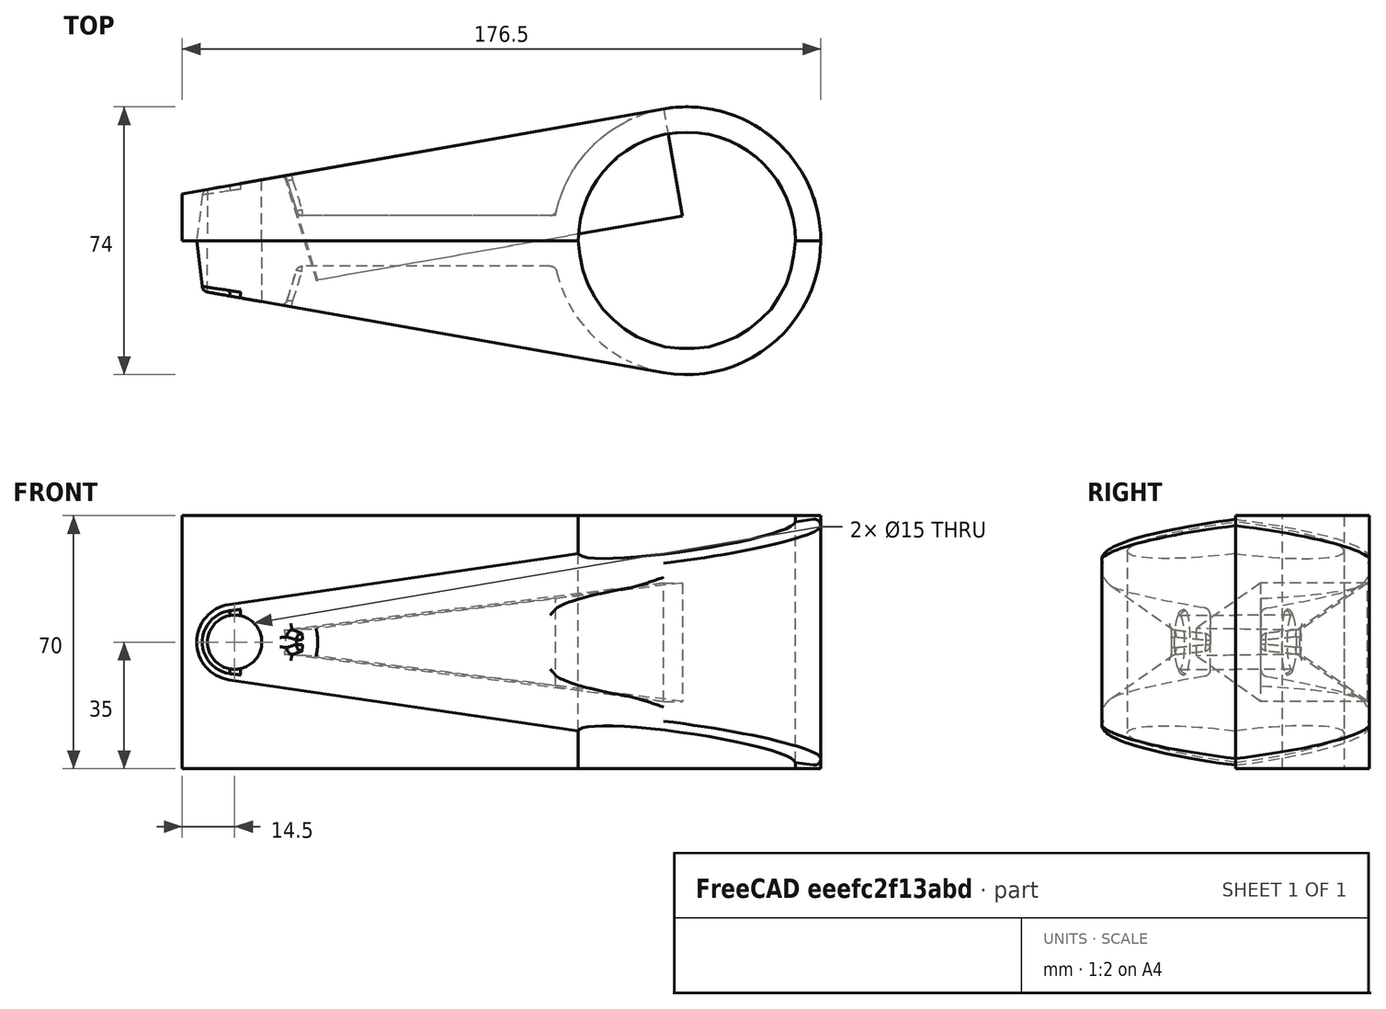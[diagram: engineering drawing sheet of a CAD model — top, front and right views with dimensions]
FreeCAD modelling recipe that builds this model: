
FCSTD DOCUMENT  (FreeCAD 1.0R39319 (Git))
Label: Mania2002-S2-1
License: All rights reserved
LicenseURL: https://en.wikipedia.org/wiki/All_rights_reserved
objects: Sketcher::SketchObject×6, PartDesign::Pad×4, PartDesign::Body×4, PartDesign::Boolean×3, PartDesign::Draft×3, PartDesign::SubShapeBinder×2, Spreadsheet::Sheet×1, PartDesign::Pocket×1, PartDesign::Fillet×1, PartDesign::Mirrored×1
note: 53 computed .brp shape members not serialized (recipe doc carries the construction recipe); baked Part::Feature solids carry a one-line shape summary decoded from their .brp

FEATURE [Spreadsheet::Sheet] Spreadsheet
  cells = A1='MainDiameter; B1(LargeDiameter)=60; A2='SubDiameter; B2(SmallDiameter)=15; A3='Length; B3(Distance)=125; A4='Thickness; B4(Thickness)=7; A5='Angle; B5=7; A6='Slope; B6(Slope)=10; A7='Fillet; B7(Fillet)=3
FEATURE [Sketcher::SketchObject] Sketch  label="Main outline"
  ArcFitTolerance = 1e-06
  AttachmentSupport = -> [XY_Plane]
  FullyConstrained = true
  MakeInternals = false
  MapMode = 5
  expr: Constraints[0] = Spreadsheet.B6
  expr: Constraints[11] = Spreadsheet.B3
  expr: Constraints[12] = Spreadsheet.B2 / 2 + Spreadsheet.B4
  expr: Constraints[14] = Spreadsheet.LargeDiameter / 2
  expr: Constraints[17] = Spreadsheet.Thickness
  sketch-geometry (7):
    g0: ArcOfCircle CenterX=0 CenterY=0 CenterZ=0 NormalX=0 NormalY=0 NormalZ=1 AngleXU=0 Radius=37 StartAngle=0 EndAngle=1.74533
    g1: LineSegment StartX=-6.42498 StartY=36.4379 StartZ=0 EndX=-139.5 EndY=12.9732 EndZ=0
    g2: LineSegment StartX=-139.5 StartY=12.9732 StartZ=0 EndX=-139.5 EndY=0 EndZ=0
    g3: LineSegment StartX=-139.5 StartY=0 StartZ=0 EndX=-125 EndY=0 EndZ=0
    g4: LineSegment StartX=-125 StartY=0 StartZ=0 EndX=-30 EndY=0 EndZ=0
    g5: LineSegment StartX=30 StartY=0 StartZ=0 EndX=37 EndY=0 EndZ=0
    g6: ArcOfCircle CenterX=0 CenterY=0 CenterZ=0 NormalX=0 NormalY=0 NormalZ=1 AngleXU=0 Radius=30 StartAngle=0 EndAngle=3.14159
  constraints (20):
    c: Angle(g-1,g1) = 0.174533
    c: Tangent(g0,g1) = -1.5708
    c: Coincident(g0,g-1)
    c: Coincident(g2,g1)
    c: Vertical(g2)
    c: PointOnObject(g2,g-1)
    c: PointOnObject(g0,g-1)
    c: Coincident(g2,g3)
    c: PointOnObject(g3,g-1)
    c: Coincident(g3,g4)
    c: Coincident(g5,g0)
    c: DistanceX(g3,g-1) = 125
    c: DistanceX(g3,g3) = 14.5
    c: Coincident(g6,g0)
    c: Radius(g6) = 30
    c: Coincident(g5,g6)
    c: PointOnObject(g5,g-1)
    c: Distance(g5,g5) = 7
    c: Coincident(g4,g6)
    c: PointOnObject(g4,g-1)
FEATURE [Sketcher::SketchObject] Sketch001  label="base"
  ArcFitTolerance = 1e-06
  AttachmentSupport = -> [XY_Plane]
  FullyConstrained = true
  MakeInternals = false
  MapMode = 5
  expr: Constraints[0] = Spreadsheet.Slope
  expr: Constraints[11] = Spreadsheet.B3
  expr: Constraints[12] = Spreadsheet.B2 / 2 + Spreadsheet.B4
  expr: Constraints[14] = Spreadsheet.LargeDiameter / 2
  expr: Constraints[17] = Spreadsheet.Thickness
  sketch-geometry (7):
    g0: ArcOfCircle CenterX=0 CenterY=0 CenterZ=0 NormalX=0 NormalY=0 NormalZ=1 AngleXU=0 Radius=37 StartAngle=0 EndAngle=1.74533
    g1: LineSegment StartX=-6.42498 StartY=36.4379 StartZ=0 EndX=-139.5 EndY=12.9732 EndZ=0
    g2: LineSegment StartX=-139.5 StartY=12.9732 StartZ=0 EndX=-139.5 EndY=0 EndZ=0
    g3: LineSegment StartX=-139.5 StartY=0 StartZ=0 EndX=-125 EndY=0 EndZ=0
    g4: LineSegment StartX=-125 StartY=0 StartZ=0 EndX=-30 EndY=3.7e-15 EndZ=0
    g5: LineSegment StartX=30 StartY=0 StartZ=0 EndX=37 EndY=0 EndZ=0
    g6: ArcOfCircle CenterX=0 CenterY=0 CenterZ=0 NormalX=0 NormalY=0 NormalZ=1 AngleXU=0 Radius=30 StartAngle=0 EndAngle=3.14159
  constraints (20):
    c: Angle(g-1,g1) = 0.174533
    c: Tangent(g0,g1) = -1.5708
    c: Coincident(g0,g-1)
    c: Coincident(g2,g1)
    c: Vertical(g2)
    c: PointOnObject(g2,g-1)
    c: PointOnObject(g0,g-1)
    c: Coincident(g2,g3)
    c: PointOnObject(g3,g-1)
    c: Coincident(g3,g4)
    c: Coincident(g5,g0)
    c: DistanceX(g3,g-1) = 125
    c: DistanceX(g3,g3) = 14.5
    c: Coincident(g6,g0)
    c: Radius(g6) = 30
    c: Coincident(g5,g6)
    c: PointOnObject(g5,g-1)
    c: Distance(g5,g5) = 7
    c: Coincident(g4,g6)
    c: PointOnObject(g4,g-1)
FEATURE [PartDesign::Pad] Pad
  Direction = (0,0,1)
  Length = 70
  Length2 = 10
  Midplane = true
  Profile = -> Sketch001
  ReferenceAxis = -> Sketch001 [N_Axis]
  Refine = true
  Suppressed = false
  Type = 0
FEATURE [PartDesign::Body] Body
  AllowCompound = false
  Group = -> [Sketch,Sketch001,Pad]
  Origin = -> Origin
  Tip = -> Pad
FEATURE [Sketcher::SketchObject] Sketch003
  ArcFitTolerance = 1e-06
  AttachmentSupport = -> [XZ_Plane001]
  FullyConstrained = true
  MakeInternals = false
  MapMode = 5
  Placement = pos=(0,0,0) rot=(1,0,0;1.5708rad)
  expr: Constraints[5] = Spreadsheet.Distance
  sketch-geometry (4):
    g0: LineSegment StartX=42 StartY=35 StartZ=0 EndX=42 EndY=-35 EndZ=0
    g1: LineSegment StartX=42 StartY=-35 StartZ=0 EndX=-126.517 EndY=-10.3898 EndZ=0
    g2: ArcOfCircle CenterX=-125 CenterY=0 CenterZ=0 NormalX=0 NormalY=0 NormalZ=1 AngleXU=0 Radius=10.5 StartAngle=1.71581 EndAngle=4.56737
    g3: LineSegment StartX=-126.517 StartY=10.3898 StartZ=0 EndX=42 EndY=35 EndZ=0
  constraints (9):
    c: Coincident(g-3,g0)
    c: Coincident(g0,g-3)
    c: Coincident(g0,g1)
    c: Coincident(g3,g0)
    c: Tangent(g2,g-4)
    c: DistanceX(g2,g-1) = 125
    c: Tangent(g2,g3) = 1.5708
    c: Tangent(g1,g2) = 1.5708
    c: PointOnObject(g2,g-1)
FEATURE [PartDesign::Pad] Pad002
  Direction = (0,-1,2e-16)
  Length = 50
  Length2 = 10
  Placement = pos=(0,0,0) rot=(1,0,0;1.5708rad)
  Profile = -> Sketch003
  ReferenceAxis = -> Sketch003 [N_Axis]
  Refine = true
  Reversed = true
  Suppressed = false
  Type = 0
FEATURE [PartDesign::Boolean] Boolean
  BaseFeature = -> Pad002
  Group = -> [Body]
  Refine = true
  Suppressed = false
  Type = 2
  UsePlacement = true
FEATURE [PartDesign::Draft] Draft
  Angle = 7
  Base = -> Boolean [?Face8,Face1,Face8]
  BaseFeature = -> Boolean
  NeutralPlane = -> Boolean [Face2]
  Refine = true
  SupportTransform = false
  Suppressed = false
FEATURE [PartDesign::SubShapeBinder] Binder
  BindCopyOnChange = 0
  BindMode = 0
  ClaimChildren = false
  Context = -> Body001 [Boolean002.Body003.Boolean001.Body002.Binder.]
  Fuse = false
  MakeFace = true
  OffsetFill = false
  OffsetIntersection = false
  OffsetJoinType = 0
  OffsetOpenResult = false
  PartialLoad = false
  Refine = true
  Relative = true
  Support = -> [Body001[Boolean.Body.Sketch001.]]
  _Version = 2
FEATURE [Sketcher::SketchObject] Sketch005
  ArcFitTolerance = 1e-06
  AttachmentSupport = -> [XY_Plane002]
  ExternalGeometry = -> [Binder]
  FullyConstrained = true
  MakeInternals = false
  MapMode = 5
  sketch-geometry (4):
    g0: LineSegment StartX=-139.5 StartY=7 StartZ=0 EndX=-36.3318 EndY=7 EndZ=0
    g1: LineSegment StartX=-6.42498 StartY=36.4379 StartZ=0 EndX=-139.5 EndY=12.9732 EndZ=0
    g2: LineSegment StartX=-139.5 StartY=12.9732 StartZ=0 EndX=-139.5 EndY=7 EndZ=0
    g3: ArcOfCircle CenterX=0 CenterY=0 CenterZ=0 NormalX=0 NormalY=0 NormalZ=1 AngleXU=0 Radius=37 StartAngle=1.74533 EndAngle=2.95126
  constraints (10):
    c: PointOnObject(g0,g-5)
    c: Horizontal(g0)
    c: Coincident(g1,g2)
    c: Coincident(g2,g0)
    c: Distance(g-1,g0) = 7
    c: Coincident(g1,g-5)
    c: Coincident(g3,g-1)
    c: Coincident(g3,g1)
    c: Coincident(g3,g0)
    c: Coincident(g1,g-4)
FEATURE [PartDesign::Pad] Pad003
  Direction = (0,0,1)
  Length = 70
  Length2 = 10
  Midplane = true
  Profile = -> Sketch005
  ReferenceAxis = -> Sketch005 [N_Axis]
  Refine = true
  Suppressed = false
  Type = 0
FEATURE [PartDesign::SubShapeBinder] Binder001
  BindCopyOnChange = 0
  BindMode = 0
  ClaimChildren = false
  Context = -> Body001 [Boolean002.Body003.Binder001.]
  Fuse = false
  MakeFace = true
  OffsetFill = false
  OffsetIntersection = false
  OffsetJoinType = 0
  OffsetOpenResult = false
  PartialLoad = false
  Refine = true
  Relative = true
  Support = -> [Body001[Pocket.Face6]]
  _Version = 2
FEATURE [Sketcher::SketchObject] Sketch006
  ArcFitTolerance = 1e-06
  AttachmentSupport = -> [Binder001]
  ExternalGeometry = -> [Binder001]
  FullyConstrained = true
  MakeInternals = false
  MapMode = 5
  Placement = pos=(-6.42498,36.4379,0) rot=(-0.061746,0.705758,0.705758;3.26493rad)
  expr: Constraints[13] = Spreadsheet.Thickness
  expr: Constraints[7] = Spreadsheet.Thickness
  sketch-geometry (6):
    g0: LineSegment StartX=6e-16 StartY=16.3544 StartZ=0 EndX=6e-16 EndY=-16.3544 EndZ=0
    g1: LineSegment StartX=6e-16 StartY=16.3544 StartZ=0 EndX=106.482 EndY=3.33452 EndZ=0
    g2: LineSegment StartX=6e-16 StartY=-16.3544 StartZ=0 EndX=106.482 EndY=-3.33452 EndZ=0
    g3: ArcOfCircle CenterX=120.593 CenterY=-6.9e-15 CenterZ=0 NormalX=0 NormalY=0 NormalZ=1 AngleXU=0 Radius=14.5 StartAngle=2.90955 EndAngle=3.37364
    g4: GeomPoint X=113.093 Y=0 Z=0
    g5: GeomPoint X=106.093 Y=0 Z=0
  constraints (15):
    c: PointOnObject(g0,g-3)
    c: Coincident(g1,g0)
    c: Coincident(g2,g0)
    c: Coincident(g3,g-6)
    c: Coincident(g3,g1)
    c: Parallel(g1,g-4)
    c: Coincident(g2,g3)
    c: Distance(g-5,g2) = 7
    c: Parallel(g2,g-5)
    c: PointOnObject(g4,g-6)
    c: PointOnObject(g5,g3)
    c: PointOnObject(g5,g-1)
    c: PointOnObject(g4,g-1)
    c: Distance(g5,g4) = 7
    c: Symmetric(g0,g0,g-1)
FEATURE [PartDesign::Pad] Pad004
  Direction = (-0.173648,0.984808,3e-16)
  Length = 30
  Length2 = 10
  Profile = -> Sketch006
  ReferenceAxis = -> Sketch006 [N_Axis]
  Refine = true
  Reversed = true
  Suppressed = false
  Type = 0
FEATURE [PartDesign::Draft] Draft001
  Angle = 7
  Base = -> Pad004 [Face3]
  BaseFeature = -> Pad004
  Refine = true
  Reversed = true
  SupportTransform = false
  Suppressed = false
FEATURE [PartDesign::Body] Body003
  AllowCompound = false
  Group = -> [Binder001,Sketch006,Pad004,Draft001]
  Origin = -> Origin003
  Tip = -> Draft001
FEATURE [Sketcher::SketchObject] Sketch007
  ArcFitTolerance = 1e-06
  AttachmentSupport = -> [Draft]
  ExternalGeometry = -> [Draft]
  FullyConstrained = true
  MakeInternals = false
  MapMode = 5
  Placement = pos=(0,0,0) rot=(1,0,0;1.5708rad)
  expr: Constraints[1] = Spreadsheet.SmallDiameter
  sketch-geometry (1):
    g0: Circle CenterX=-125 CenterY=0 CenterZ=0 NormalX=0 NormalY=0 NormalZ=1 AngleXU=0 Radius=7.5
  constraints (2):
    c: Coincident(g0,g-3)
    c: Diameter(g0) = 15
FEATURE [PartDesign::Pocket] Pocket
  BaseFeature = -> Draft
  Direction = (0,1,-2e-16)
  Length = 5
  Length2 = 5
  Profile = -> Sketch007
  ReferenceAxis = -> Sketch007 [N_Axis]
  Refine = true
  Suppressed = false
  Type = 1
FEATURE [PartDesign::Boolean] Boolean001
  BaseFeature = -> Pad003
  Group = -> [Body003]
  Refine = true
  Suppressed = false
  Type = 2
  UsePlacement = true
FEATURE [PartDesign::Body] Body002
  AllowCompound = false
  Group = -> [Binder,Sketch005,Pad003,Boolean001]
  Origin = -> Origin002
  Tip = -> Boolean001
FEATURE [PartDesign::Boolean] Boolean002
  BaseFeature = -> Pocket
  Group = -> [Body002]
  Refine = true
  Suppressed = false
  Type = 1
  UsePlacement = true
FEATURE [PartDesign::Draft] Draft002
  Angle = 7
  Base = -> Boolean002 [Face9,Face11]
  BaseFeature = -> Boolean002
  Refine = true
  Reversed = true
  SupportTransform = false
  Suppressed = false
FEATURE [PartDesign::Fillet] Fillet
  Base = -> Draft002 [Edge30,Edge29,Edge31,Edge18,Edge26,Edge19,Edge17,Edge27,Edge33,Edge21]
  BaseFeature = -> Draft002
  Radius = 1.8
  Refine = true
  SupportTransform = false
  Suppressed = false
  UseAllEdges = false
FEATURE [PartDesign::Mirrored] Mirrored
  BaseFeature = -> Fillet
  MirrorPlane = -> XZ_Plane001
  Refine = true
  Suppressed = false
  TransformMode = 1
FEATURE [PartDesign::Body] Body001
  AllowCompound = false
  Group = -> [Sketch003,Pad002,Boolean,Draft,Sketch007,Pocket,Boolean002,Draft002,Fillet,Mirrored]
  Origin = -> Origin001
  Tip = -> Mirrored
